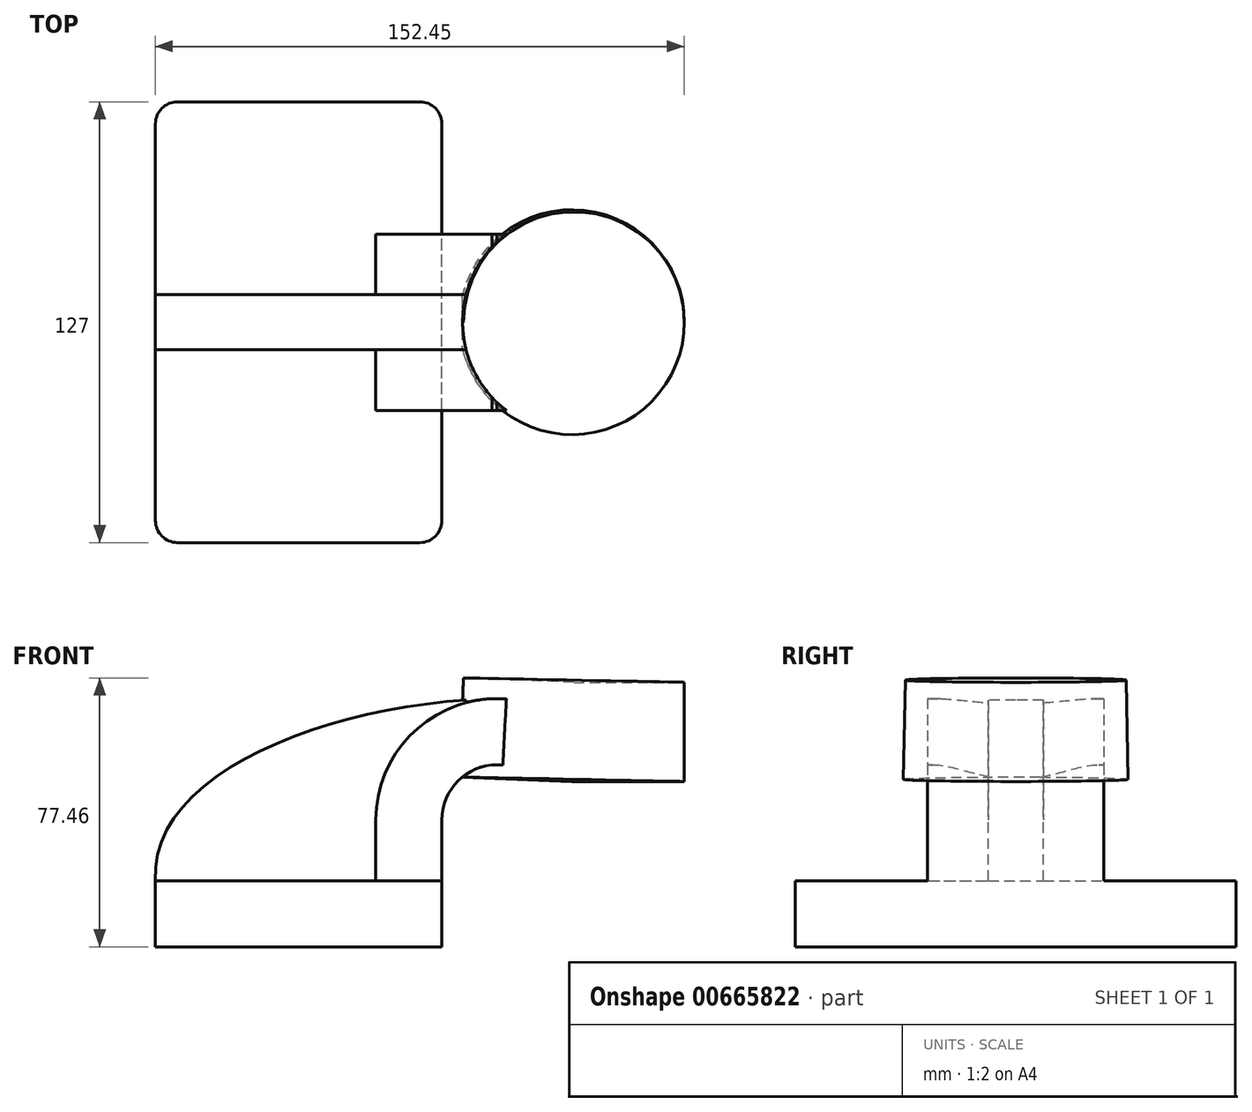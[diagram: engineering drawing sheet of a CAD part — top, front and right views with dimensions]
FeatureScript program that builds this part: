
annotation { "Feature Type Name" : "Feature", "Feature Type Description" : "" }
export const myFeature = defineFeature(function(context is Context, id is Id, definition is map)
    precondition{}
    {
        {
            var Q0;
            Q0=qCreatedBy(makeId("Front.planeOp"),FACE);
            var sketch = newSketch(context, id + "F0", { "sketchPlane" : qUnion([Q0])});
            skLineSegment(sketch, "E0.bottom", {"start": v(-41.28, 9.53) * mm, "end": v(41.28, 9.53) * mm});
            skLineSegment(sketch, "E0.top", {"start": v(-41.28, -9.53) * mm, "end": v(41.28, -9.53) * mm});
            skLineSegment(sketch, "E0.left", {"start": v(-41.28, 9.53) * mm, "end": v(-41.28, -9.53) * mm});
            skLineSegment(sketch, "E0.right", {"start": v(41.28, 9.53) * mm, "end": v(41.28, -9.53) * mm});
            skPoint(sketch, "E0.middle", {"position": v(0, 0) * mm});
            skLineSegment(sketch, "E1.bottom", {"start": v(111.12, 38.1) * mm, "end": v(60.32, 38.1) * mm});
            skLineSegment(sketch, "E1.top", {"start": v(111.12, 66.67) * mm, "end": v(60.32, 66.67) * mm});
            skLineSegment(sketch, "E1.left", {"start": v(111.12, 38.1) * mm, "end": v(111.12, 66.68) * mm});
            skLineSegment(sketch, "E1.right", {"start": v(60.32, 38.1) * mm, "end": v(60.32, 66.68) * mm});
            skPoint(sketch, "E1.middle", {"position": v(85.72, 52.39) * mm});
            skLineSegment(sketch, "E2", {"start": v(41.28, 9.53) * mm, "end": v(41.28, 27.05) * mm});
            skArc(sketch, "E3", {"start": v(41.28, 27.05) * mm, "mid": v(45.92, 38.28) * mm, "end": v(57.15, 42.93) * mm});
            skLineSegment(sketch, "E4", {"start": v(57.15, 42.93) * mm, "end": v(79.3, 42.93) * mm});
            skLineSegment(sketch, "E5.0", {"start": v(57.15, 61.98) * mm, "end": v(79.3, 61.98) * mm});
            skArc(sketch, "E5.1", {"start": v(22.23, 27.05) * mm, "mid": v(32.45, 51.75) * mm, "end": v(57.15, 61.98) * mm});
            skLineSegment(sketch, "E5.2", {"start": v(22.23, 9.53) * mm, "end": v(22.23, 27.05) * mm});
            skFitSpline(sketch, "E6", {"points": [v(-41.28, 9.53) * mm, v(57.15, 61.98) * mm], "startDerivative": vector(-5.72, 96.3) * mm, "endDerivative": vector(136.29, 2.26) * mm});
            skLineSegment(sketch, "E7", {"start": v(78.73, 38.1) * mm, "end": v(79.3, 66.67) * mm});
            skSolve(sketch);
        }
        {
            var Q0;
            Q0=makeQuery(id+"F0.imprint","IMPRINT",FACE,{"disambiguationData":[TD([[makeQuery(id+"F0.imprint","IMPRINT",EDGE,{"derivedFrom":sQuery(id+"F0.wireOp",EDGE,"E0.top")}),1.0]])]});
            extrude(context, id + "F1", {"entities" : qUnion([Q0]), "endBound" : BoundingType.SYMMETRIC, "depth" : 127 * mm, "offsetDistance" : 25.4 * mm});
        }
        {
            var Q0;
            {var subQ1=sQuery(id+"F0.wireOp",EDGE,"E2");Q0=makeQuery(id+"F0.imprint","IMPRINT",FACE,{"disambiguationData":[TD([[makeQuery(id+"F0.imprint","IMPRINT",EDGE,{"derivedFrom":subQ1}),1.0]])]});}
            var Q1;
            {var subQ5=sQuery(id+"F0.wireOp",EDGE,"wcSvzukb-4Mda-VN0V-8Yzv-vmF5kc4wjIuy");Q1=makeQuery(id+"F0.imprint","IMPRINT",FACE,{"disambiguationData":[TD([[makeQuery(id+"F0.imprint","IMPRINT",EDGE,{"derivedFrom":subQ5}),1.0]])]});}
            extrude(context, id + "F2", {"entities" : qUnion([Q0, Q1]), "operationType" : NewBodyOperationType.ADD, "endBound" : BoundingType.SYMMETRIC, "depth" : 50.8 * mm, "offsetDistance" : 25.4 * mm});
        }
        {
            var Q0;
            {var subQ3=sQuery(id+"F0.wireOp",EDGE,"E5.2");Q0=makeQuery(id+"F0.imprint","IMPRINT",FACE,{"disambiguationData":[TD([[makeQuery(id+"F0.imprint","IMPRINT",EDGE,{"derivedFrom":subQ3}),1.0]])]});}
            extrude(context, id + "F3", {"entities" : qUnion([Q0]), "operationType" : NewBodyOperationType.ADD, "endBound" : BoundingType.SYMMETRIC, "depth" : 15.88 * mm, "offsetDistance" : 25.4 * mm});
        }
        {
            var Q0;
            {var subQ0=sQuery(id+"F0.wireOp",EDGE,"E4");var subQ1=sQuery(id+"F0.wireOp",EDGE,"E1.right");var subQ2=makeQuery(id+"F0.imprint","INTERSECT",VERTEX,{"derivedFrom":[subQ1,subQ0]});Q0=makeQuery(id+"F0.imprint","IMPRINT",FACE,{"disambiguationData":[TD([[makeQuery(id+"F0.imprint","IMPRINT",EDGE,{"disambiguationData":[TD([[subQ2,-1.0]])],"derivedFrom":subQ1}),-1.0]])]});}
            extrude(context, id + "F4", {"entities" : qUnion([Q0]), "operationType" : NewBodyOperationType.ADD, "endBound" : BoundingType.SYMMETRIC, "depth" : 50.8 * mm, "offsetDistance" : 25.4 * mm});
        }
        {
            var Q0;
            {var subQ4=sQuery(id+"F0.wireOp",EDGE,"E1.left");Q0=makeQuery(id+"F0.imprint","IMPRINT",FACE,{"disambiguationData":[TD([[makeQuery(id+"F0.imprint","IMPRINT",EDGE,{"derivedFrom":subQ4}),1.0]])]});}
            var Q1;
            Q1=sQuery(id+"F0.wireOp",EDGE,"E7");
            revolve(context, id + "F5", {"operationType" : NewBodyOperationType.ADD, "entities" : qUnion([Q0]), "axis" : qUnion([Q1]), "revolveType" : RevolveType.FULL});
        }
        {
            var Q0;
            Q0=makeQuery(id+"F1.opExtrude","CAP_EDGE",EDGE,{"disambiguationData":[OSD([sQuery(id+"F0.wireOp",EDGE,"E0.right")])],"isStart":false});
            var Q1;
            Q1=makeQuery(id+"F1.opExtrude","CAP_EDGE",EDGE,{"disambiguationData":[OSD([sQuery(id+"F0.wireOp",EDGE,"E0.left")])],"isStart":false});
            var Q2;
            Q2=makeQuery(id+"F1.opExtrude","CAP_EDGE",EDGE,{"disambiguationData":[OSD([sQuery(id+"F0.wireOp",EDGE,"E0.left")])],"isStart":true});
            var Q3;
            Q3=makeQuery(id+"F1.opExtrude","CAP_EDGE",EDGE,{"disambiguationData":[OSD([sQuery(id+"F0.wireOp",EDGE,"E0.right")])],"isStart":true});
            fillet(context, id + "F6", {"entities" : qUnion([Q0, Q1, Q2, Q3]), "radius" : 6.35 * mm, "tangentPropagation" : true, "allowEdgeOverflow" : false});
        }
    });
